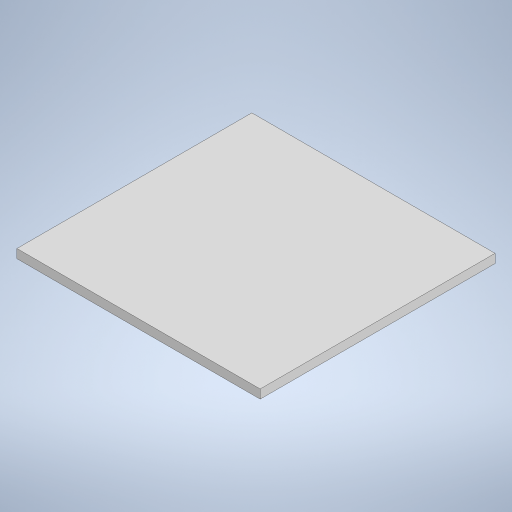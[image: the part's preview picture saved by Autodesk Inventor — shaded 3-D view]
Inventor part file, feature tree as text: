
AUTODESK INVENTOR PART (.ipt)
format: ipt  version: 2024.1 (Build 281209000, 209)  size: 188,416 bytes
history: native  units: mm
features: extrude x1, sketch x1
ambient origin geometry x8: Origin, YZ Plane, XZ Plane, XY Plane, X Axis, Y Axis, Z Axis, Center Point
bodies: Solid1 (feature_tree)
feature tree (2):
  extrude  "Extrusion1"  Depth=350.0mm
  sketch  "Sketch1"  dims[d0=338.0mm d1=350.0mm d2=12.7mm d3=0.0mm]
